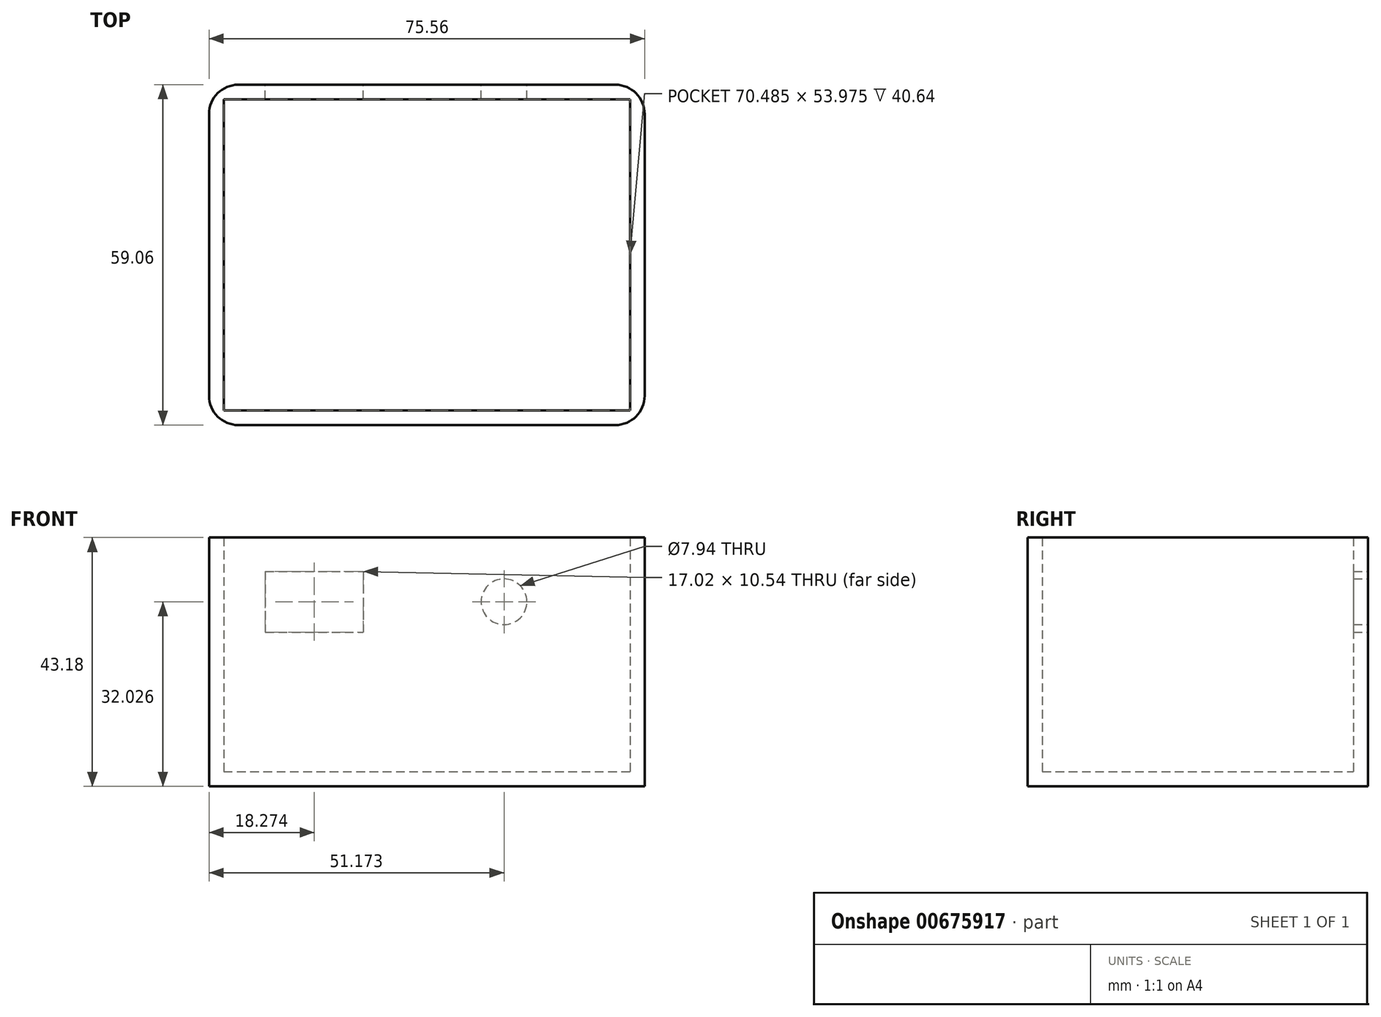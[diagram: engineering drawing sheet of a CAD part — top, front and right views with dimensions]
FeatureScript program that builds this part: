
annotation { "Feature Type Name" : "Feature", "Feature Type Description" : "" }
export const myFeature = defineFeature(function(context is Context, id is Id, definition is map)
    precondition{}
    {
        {
            var Q0;
            Q0=qCreatedBy(makeId("Top.planeOp"),FACE);
            var sketch = newSketch(context, id + "F0", { "sketchPlane" : qUnion([Q0])});
            skLineSegment(sketch, "E0.bottom", {"start": v(-37.78, -29.53) * mm, "end": v(37.78, -29.53) * mm});
            skLineSegment(sketch, "E0.top", {"start": v(-37.78, 29.53) * mm, "end": v(37.78, 29.53) * mm});
            skLineSegment(sketch, "E0.left", {"start": v(-37.78, -29.53) * mm, "end": v(-37.78, 29.53) * mm});
            skLineSegment(sketch, "E0.right", {"start": v(37.78, -29.53) * mm, "end": v(37.78, 29.53) * mm});
            skPoint(sketch, "E0.middle", {"position": v(0, 0) * mm});
            skSolve(sketch);
        }
        {
            var Q0;
            Q0 = qSketchRegion(id + "F0", true);
            extrude(context, id + "F1", {"entities" : qUnion([Q0]), "depth" : 43.18 * mm, "offsetDistance" : 25.4 * mm});
        }
        {
            var Q0;
            Q0=makeQuery(id+"F1.opExtrude","CAP_FACE",FACE,{"disambiguationData":[OSD([sQuery(id+"F0.wireOp",EDGE,"E0.bottom"),sQuery(id+"F0.wireOp",EDGE,"E0.top"),sQuery(id+"F0.wireOp",EDGE,"E0.left"),sQuery(id+"F0.wireOp",EDGE,"E0.right")])],"isStart":false});
            shell(context, id + "F2", {"entities" : qUnion([Q0]), "thickness" : 2.54 * mm});
        }
        {
            var Q0;
            Q0=makeQuery(id+"F1.opExtrude","SWEPT_FACE",FACE,{"disambiguationData":[OSD([sQuery(id+"F0.wireOp",EDGE,"E0.top")])]});
            var sketch = newSketch(context, id + "F3", { "sketchPlane" : qUnion([Q0])});
            skLineSegment(sketch, "E1.bottom", {"start": v(28.01, 37.3) * mm, "end": v(11, 37.3) * mm});
            skLineSegment(sketch, "E1.top", {"start": v(28.01, 26.76) * mm, "end": v(11, 26.76) * mm});
            skLineSegment(sketch, "E1.left", {"start": v(28.01, 37.3) * mm, "end": v(28.01, 26.76) * mm});
            skLineSegment(sketch, "E1.right", {"start": v(11, 37.3) * mm, "end": v(11, 26.76) * mm});
            skPoint(sketch, "E1.middle", {"position": v(19.5, 32.03) * mm});
            skSolve(sketch);
        }
        {
            var Q0;
            Q0 = qSketchRegion(id + "F3", true);
            extrude(context, id + "F4", {"entities" : qUnion([Q0]), "operationType" : NewBodyOperationType.REMOVE, "oppositeDirection" : true, "depth" : 3.3 * mm, "offsetDistance" : 25.4 * mm});
        }
        {
            var Q0;
            Q0=makeQuery(id+"F1.opExtrude","SWEPT_FACE",FACE,{"disambiguationData":[OSD([sQuery(id+"F0.wireOp",EDGE,"E0.top")])]});
            var sketch = newSketch(context, id + "F5", { "sketchPlane" : qUnion([Q0])});
            skLineSegment(sketch, "E2", {"start": v(-13.4, 43.18) * mm, "end": v(-13.4, 32.03) * mm});
            skLineSegment(sketch, "E3", {"start": v(11, 32.03) * mm, "end": v(-37.78, 32.03) * mm});
            skSolve(sketch);
        }
        {
            var Q0;
            Q0=sQuery(id+"F5.wireOp",VERTEX,"ISpM8A6w-PKEW-MHMS-DoUG-373GydDGFNZQ.end");
            var Q1;
            Q1=sQuery(id+"F5.wireOp",VERTEX,"E2.end");
            var Q2;
            Q2=makeQuery(id+"F1.opExtrude","SWEPT_BODY",BODY,{"disambiguationData":[OSD([sQuery(id+"F0.wireOp",EDGE,"E0.bottom"),sQuery(id+"F0.wireOp",EDGE,"E0.top"),sQuery(id+"F0.wireOp",EDGE,"E0.left"),sQuery(id+"F0.wireOp",EDGE,"E0.right")])]});
            hole(context, id + "F6", {"style" : HoleStyle.SIMPLE, "endStyle" : HoleEndStyle.BLIND, "holeDiameter" : 7.94 * mm, "majorDiameter" : 6.35 * mm, "holeDepth" : 12.7 * mm, "isTappedThrough" : true, "tappedDepth" : 12.7 * mm, "tapClearance" : 3, "locations" : qUnion([Q0, Q1]), "scope" : qUnion([Q2])});
        }
        {
            var Q0;
            Q0=makeQuery(id+"F1.opExtrude","SWEPT_EDGE",EDGE,{"disambiguationData":[OSD([sQuery(id+"F0.wireOp",EDGE,"E0.bottom"),sQuery(id+"F0.wireOp",EDGE,"E0.left")])]});
            var Q1;
            Q1=makeQuery(id+"F1.opExtrude","SWEPT_EDGE",EDGE,{"disambiguationData":[OSD([sQuery(id+"F0.wireOp",EDGE,"E0.bottom"),sQuery(id+"F0.wireOp",EDGE,"E0.right")])]});
            var Q2;
            Q2=makeQuery(id+"F1.opExtrude","SWEPT_EDGE",EDGE,{"disambiguationData":[OSD([sQuery(id+"F0.wireOp",EDGE,"E0.top"),sQuery(id+"F0.wireOp",EDGE,"E0.right")])]});
            var Q3;
            Q3=makeQuery(id+"F1.opExtrude","SWEPT_EDGE",EDGE,{"disambiguationData":[OSD([sQuery(id+"F0.wireOp",EDGE,"E0.top"),sQuery(id+"F0.wireOp",EDGE,"E0.left")])]});
            fillet(context, id + "F7", {"entities" : qUnion([Q0, Q1, Q2, Q3]), "radius" : 5.08 * mm, "tangentPropagation" : true, "allowEdgeOverflow" : false});
        }
    });
